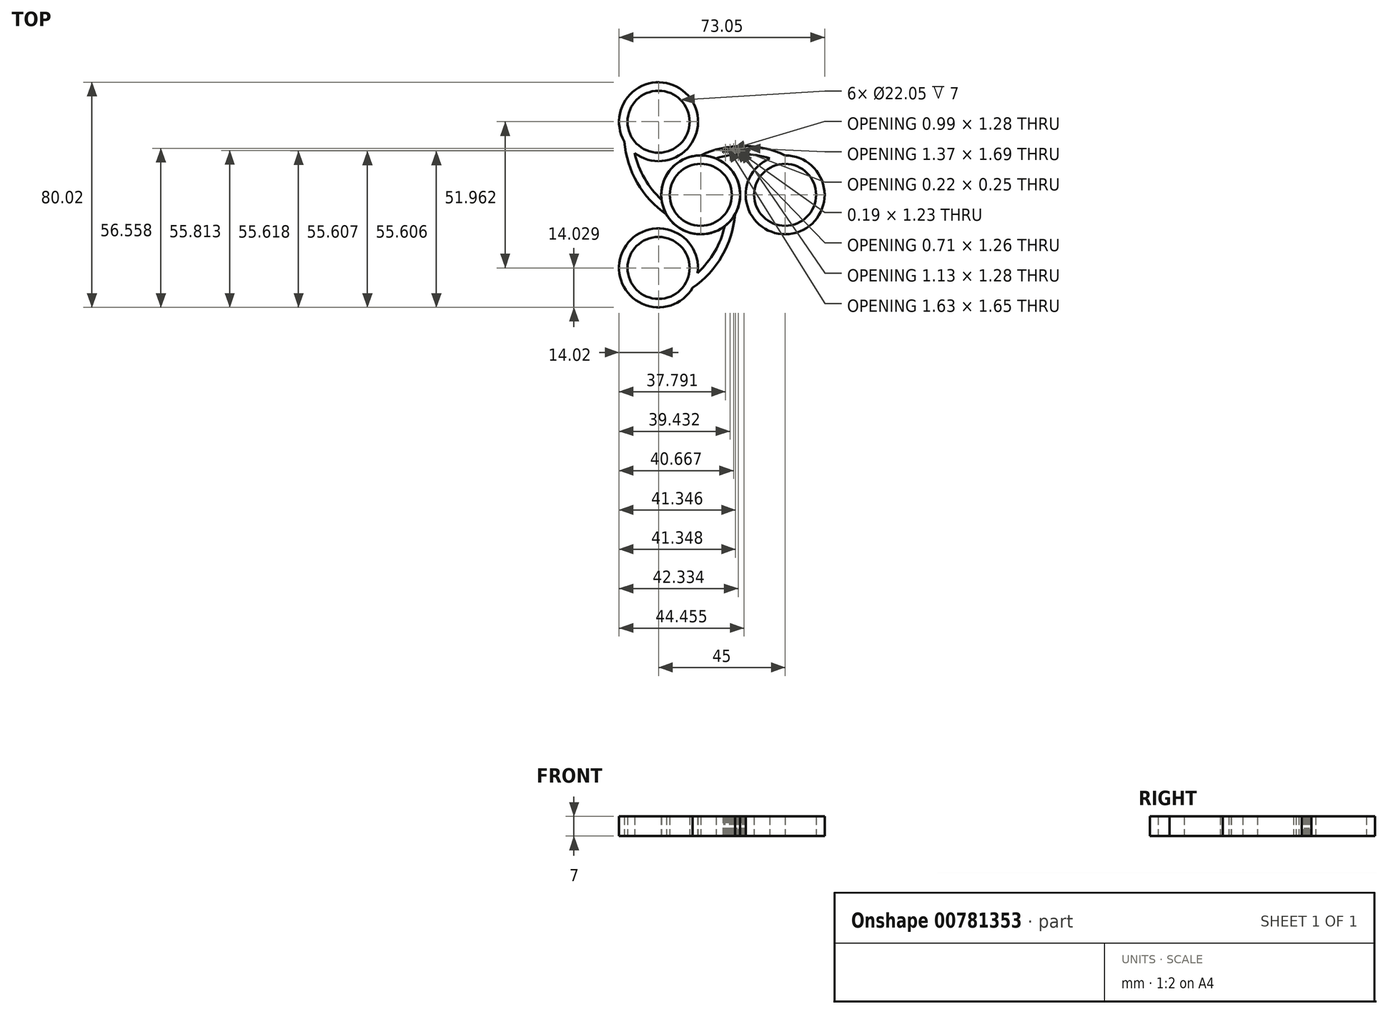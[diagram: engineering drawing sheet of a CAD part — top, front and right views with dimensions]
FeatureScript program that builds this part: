
annotation { "Feature Type Name" : "Feature", "Feature Type Description" : "" }
export const myFeature = defineFeature(function(context is Context, id is Id, definition is map)
    precondition{}
    {
        {
            var Q0;
            Q0=qCreatedBy(makeId("Top.planeOp"),FACE);
            var sketch = newSketch(context, id + "F0", { "sketchPlane" : qUnion([Q0])});
            skCircle(sketch, "E0", {"center": v(0, 0) * mm, "radius": 11.03 * mm});
            skCircle(sketch, "E1.0", {"center": v(0, 0) * mm, "radius": 14.02 * mm});
            skCircle(sketch, "E2.1.0.0", {"center": v(30, 0) * mm, "radius": 11.03 * mm});
            skCircle(sketch, "E2.1.0.1", {"center": v(30, 0) * mm, "radius": 14.02 * mm});
            skLineSegment(sketch, "E2.direction1", {"start": v(0, 0) * mm, "end": v(30, 0) * mm, "construction": true});
            skLineSegment(sketch, "E3", {"start": v(30, 25.13) * mm, "end": v(30, -41.78) * mm});
            skArc(sketch, "E4", {"start": v(30, 14.03) * mm, "mid": v(15, 17.4) * mm, "end": v(0, 14.02) * mm});
            skArc(sketch, "E5.0", {"start": v(28.71, 11.31) * mm, "mid": v(15, 14.4) * mm, "end": v(1.29, 11.31) * mm});
            skArc(sketch, "E6.MirrorCS", {"start": v(28.71, -11.31) * mm, "mid": v(15, -14.4) * mm, "end": v(1.29, -11.31) * mm});
            skArc(sketch, "E7.MirrorCS", {"start": v(30, -14.03) * mm, "mid": v(15, -17.4) * mm, "end": v(0, -14.02) * mm});
            skSolve(sketch);
        }
        {
            var Q0;
            {var subQ0=sQuery(id+"F0.wireOp",EDGE,"E3");var subQ1=sQuery(id+"F0.wireOp",EDGE,"E2.1.0.0");var subQ2=makeQuery(id+"F0.imprint","INTERSECT",VERTEX,{"disambiguationData":[OD(0.0)],"derivedFrom":[subQ1,subQ0]});Q0=makeQuery(id+"F0.imprint","IMPRINT",FACE,{"disambiguationData":[TD([[makeQuery(id+"F0.imprint","IMPRINT",EDGE,{"disambiguationData":[TD([[subQ2,1.0]])],"derivedFrom":subQ1}),-1.0]])]});}
            var Q1;
            {var subQ0=sQuery(id+"F0.wireOp",EDGE,"E3");var subQ6=sQuery(id+"F0.wireOp",EDGE,"E2.1.0.0");var subQ7=makeQuery(id+"F0.imprint","INTERSECT",VERTEX,{"disambiguationData":[OD(0.0)],"derivedFrom":[subQ6,subQ0]});Q1=makeQuery(id+"F0.imprint","IMPRINT",FACE,{"disambiguationData":[TD([[makeQuery(id+"F0.imprint","IMPRINT",EDGE,{"disambiguationData":[TD([[subQ7,-1.0]])],"derivedFrom":subQ6}),-1.0]])]});}
            var Q2;
            {var subQ0=sQuery(id+"F0.wireOp",EDGE,"E4");Q2=makeQuery(id+"F0.imprint","IMPRINT",FACE,{"disambiguationData":[TD([[makeQuery(id+"F0.imprint","IMPRINT",EDGE,{"derivedFrom":subQ0}),1.0]])]});}
            var Q3;
            {var subQ0=sQuery(id+"F0.wireOp",EDGE,"E7.MirrorCS");Q3=makeQuery(id+"F0.imprint","IMPRINT",FACE,{"disambiguationData":[TD([[makeQuery(id+"F0.imprint","IMPRINT",EDGE,{"derivedFrom":subQ0}),-1.0]])]});}
            var Q4;
            Q4=makeQuery(id+"F0.imprint","IMPRINT",FACE,{"disambiguationData":[TD([[makeQuery(id+"F0.imprint","IMPRINT",EDGE,{"derivedFrom":sQuery(id+"F0.wireOp",EDGE,"E0")}),-1.0]])]});
            extrude(context, id + "F1", {"entities" : qUnion([Q0, Q1, Q2, Q3, Q4]), "depth" : 7 * mm, "offsetDistance" : 25 * mm});
        }
        {
            var Q0;
            Q0=makeQuery(id+"F1.opExtrude","SWEPT_BODY",BODY,{"disambiguationData":[OSD([sQuery(id+"F0.wireOp",EDGE,"E0"),sQuery(id+"F0.wireOp",EDGE,"E1.0"),sQuery(id+"F0.wireOp",EDGE,"ddfe1a80-111f-40ba-aa11-5838728418130.MirrorC"),sQuery(id+"F0.wireOp",EDGE,"ddfe1a80-111f-40ba-aa11-5838728418131.MirrorC"),sQuery(id+"F0.wireOp",EDGE,"WN3oxOSN-cVLn-UZjw-D7Z1-LqRepIl2l9xi"),sQuery(id+"F0.wireOp",EDGE,"065204ab-c5dd-4cf8-a66f-a6cb3593be3f0.MirrorCS")])]});
            var Q1;
            Q1=makeQuery(id+"F1.opExtrude","CAP_EDGE",EDGE,{"disambiguationData":[OSD([sQuery(id+"F0.wireOp",EDGE,"E0")])],"isStart":false});
            circularPattern(context, id + "F2", {"entities" : qUnion([Q0]), "axis" : qUnion([Q1]), "angle" : 360 * degree, "instanceCount" : 3, "equalSpace" : true});
        }
        {
            var Q0;
            Q0=makeQuery(id+"F1.opExtrude","CAP_FACE",FACE,{"disambiguationData":[OSD([sQuery(id+"F0.wireOp",EDGE,"E0"),sQuery(id+"F0.wireOp",EDGE,"E1.0"),sQuery(id+"F0.wireOp",EDGE,"E2.1.0.0"),sQuery(id+"F0.wireOp",EDGE,"E2.1.0.1"),sQuery(id+"F0.wireOp",EDGE,"E4"),sQuery(id+"F0.wireOp",EDGE,"E5.0"),sQuery(id+"F0.wireOp",EDGE,"E6.MirrorCS"),sQuery(id+"F0.wireOp",EDGE,"E7.MirrorCS")])],"isStart":false});
            var sketch = newSketch(context, id + "F3", { "sketchPlane" : qUnion([Q0])});
            skText(sketch, "E8", { "text": "Mario G", "fontName": "OpenSans-Regular.ttf"});
            const initialGuessF3  = {"E8": [0.00773, 0.01498, 1, 0, 0.00166]};
            skSetInitialGuess(sketch, initialGuessF3);
            skSolve(sketch);
        }
        {
            var Q0;
            Q0=qSketchRegion(id+"F3",true);
            extrude(context, id + "F4", {"entities" : qUnion([Q0]), "operationType" : NewBodyOperationType.REMOVE, "oppositeDirection" : true, "depth" : 20 * mm, "offsetDistance" : 25 * mm});
        }
    });
